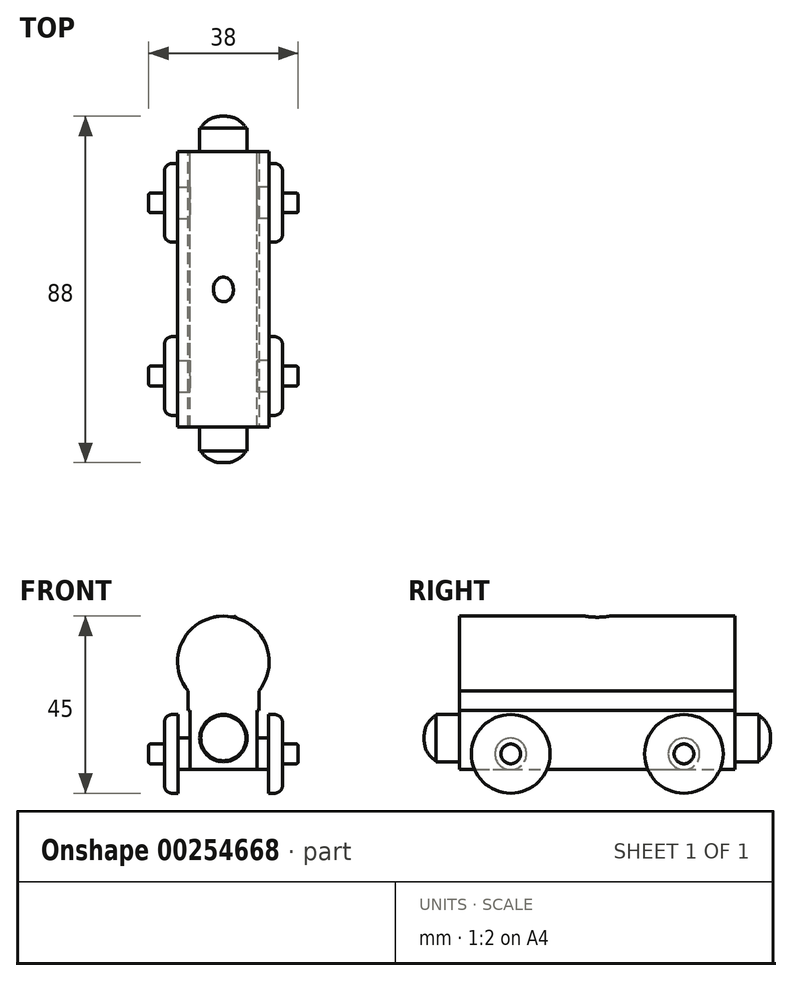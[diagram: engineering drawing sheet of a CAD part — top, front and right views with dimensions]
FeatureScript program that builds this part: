
annotation { "Feature Type Name" : "Feature", "Feature Type Description" : "" }
export const myFeature = defineFeature(function(context is Context, id is Id, definition is map)
    precondition{}
    {
        {
            var Q0;
            Q0=qCreatedBy(makeId("Front.planeOp"),FACE);
            var sketch = newSketch(context, id + "F0", { "sketchPlane" : qUnion([Q0])});
            skLineSegment(sketch, "E0", {"start": v(-9, -7.37) * mm, "end": v(9, -7.37) * mm});
            skArc(sketch, "E1", {"start": v(9, -7.37) * mm, "mid": v(0, 11.63) * mm, "end": v(-9, -7.37) * mm});
            skLineSegment(sketch, "E2", {"start": v(0, 19.14) * mm, "end": v(0, -28.25) * mm, "construction": true});
            skPoint(sketch, "E2.startSnap0", {"position": v(0, 11.63) * mm});
            skSolve(sketch);
        }
        {
            var Q0;
            Q0 = qSketchRegion(id + "F0", true);
            extrude(context, id + "F1", {"entities" : qUnion([Q0]), "endBound" : BoundingType.SYMMETRIC, "depth" : 70 * mm});
        }
        {
            var Q0;
            Q0=makeQuery(id+"F1.opExtrude","CAP_FACE",FACE,{"disambiguationData":[OSD([sQuery(id+"F0.wireOp",EDGE,"E0"),sQuery(id+"F0.wireOp",EDGE,"E1")])],"isStart":false});
            var sketch = newSketch(context, id + "F2", { "sketchPlane" : qUnion([Q0])});
            skLineSegment(sketch, "E3.bottom", {"start": v(-9, -7.37) * mm, "end": v(9, -7.37) * mm});
            skLineSegment(sketch, "E3.top", {"start": v(-9, -12.37) * mm, "end": v(9, -12.37) * mm});
            skLineSegment(sketch, "E3.left", {"start": v(-9, -7.37) * mm, "end": v(-9, -12.37) * mm});
            skLineSegment(sketch, "E3.right", {"start": v(9, -7.37) * mm, "end": v(9, -12.37) * mm});
            skSolve(sketch);
        }
        {
            var Q0;
            Q0 = qSketchRegion(id + "F2", true);
            extrude(context, id + "F3", {"entities" : qUnion([Q0]), "oppositeDirection" : true, "depth" : 70 * mm});
        }
        {
            var Q0;
            Q0=makeQuery(id+"F1.opExtrude","SWEPT_BODY",BODY,{"disambiguationData":[OSD([sQuery(id+"F0.wireOp",EDGE,"E0"),sQuery(id+"F0.wireOp",EDGE,"E1")])]});
            var Q1;
            Q1=makeQuery(id+"F3.opExtrude","SWEPT_BODY",BODY,{"disambiguationData":[OSD([sQuery(id+"F2.wireOp",EDGE,"E3.bottom"),sQuery(id+"F2.wireOp",EDGE,"E3.top"),sQuery(id+"F2.wireOp",EDGE,"E3.left"),sQuery(id+"F2.wireOp",EDGE,"E3.right")])]});
            booleanBodies(context, id + "F4", {"operationType" : BooleanOperationType.UNION, "tools" : qUnion([Q0, Q1])});
        }
        {
            var Q0;
            Q0=makeQuery(id+"F3.opExtrude","SWEPT_FACE",FACE,{"disambiguationData":[OSD([sQuery(id+"F2.wireOp",EDGE,"E3.top")])]});
            var sketch = newSketch(context, id + "F5", { "sketchPlane" : qUnion([Q0])});
            skLineSegment(sketch, "E4.bottom", {"start": v(-8.5, 35) * mm, "end": v(8.5, 35) * mm});
            skLineSegment(sketch, "E4.top", {"start": v(-8.5, -35) * mm, "end": v(8.5, -35) * mm});
            skLineSegment(sketch, "E4.left", {"start": v(-8.5, 35) * mm, "end": v(-8.5, -35) * mm});
            skLineSegment(sketch, "E4.right", {"start": v(8.5, 35) * mm, "end": v(8.5, -35) * mm});
            skSolve(sketch);
        }
        {
            var Q0;
            Q0 = qSketchRegion(id + "F5", true);
            extrude(context, id + "F6", {"entities" : qUnion([Q0]), "operationType" : NewBodyOperationType.ADD, "depth" : 15 * mm});
        }
        {
            var Q0;
            Q0=makeQuery(id+"F6.boolean.opBoolean","MERGE",FACE,{"derivedFrom":[makeQuery(id+"F4.opBoolean","MERGE",FACE,{"derivedFrom":[makeQuery(id+"F1.opExtrude","CAP_FACE",FACE,{"disambiguationData":[OSD([sQuery(id+"F0.wireOp",EDGE,"E0"),sQuery(id+"F0.wireOp",EDGE,"E1")])],"isStart":false}),makeQuery(id+"F3.opExtrude","CAP_FACE",FACE,{"disambiguationData":[OSD([sQuery(id+"F2.wireOp",EDGE,"E3.bottom"),sQuery(id+"F2.wireOp",EDGE,"E3.top"),sQuery(id+"F2.wireOp",EDGE,"E3.left"),sQuery(id+"F2.wireOp",EDGE,"E3.right")])],"isStart":true})]}),makeQuery(id+"F6.opExtrude","SWEPT_FACE",FACE,{"disambiguationData":[OSD([sQuery(id+"F5.wireOp",EDGE,"E4.bottom")])]})]});
            var sketch = newSketch(context, id + "F7", { "sketchPlane" : qUnion([Q0])});
            skCircle(sketch, "E5", {"center": v(0, -19.37) * mm, "radius": 6 * mm});
            skSolve(sketch);
        }
        {
            var Q0;
            Q0 = qSketchRegion(id + "F7", true);
            extrude(context, id + "F8", {"entities" : qUnion([Q0]), "operationType" : NewBodyOperationType.ADD, "depth" : 6 * mm});
        }
        {
            var Q0;
            Q0=makeQuery(id+"F6.boolean.opBoolean","MERGE",FACE,{"derivedFrom":[makeQuery(id+"F4.opBoolean","MERGE",FACE,{"derivedFrom":[makeQuery(id+"F1.opExtrude","CAP_FACE",FACE,{"disambiguationData":[OSD([sQuery(id+"F0.wireOp",EDGE,"E0"),sQuery(id+"F0.wireOp",EDGE,"E1")])],"isStart":true}),makeQuery(id+"F3.opExtrude","CAP_FACE",FACE,{"disambiguationData":[OSD([sQuery(id+"F2.wireOp",EDGE,"E3.bottom"),sQuery(id+"F2.wireOp",EDGE,"E3.top"),sQuery(id+"F2.wireOp",EDGE,"E3.left"),sQuery(id+"F2.wireOp",EDGE,"E3.right")])],"isStart":false})]}),makeQuery(id+"F6.opExtrude","SWEPT_FACE",FACE,{"disambiguationData":[OSD([sQuery(id+"F5.wireOp",EDGE,"E4.top")])]})]});
            var sketch = newSketch(context, id + "F9", { "sketchPlane" : qUnion([Q0])});
            skCircle(sketch, "E6", {"center": v(0, -19.37) * mm, "radius": 6 * mm});
            skSolve(sketch);
        }
        {
            var Q0;
            Q0 = qSketchRegion(id + "F9", true);
            extrude(context, id + "F10", {"entities" : qUnion([Q0]), "operationType" : NewBodyOperationType.ADD, "depth" : 6 * mm});
        }
        {
            var Q0;
            Q0=qCreatedBy(makeId("Front.planeOp"),FACE);
            var sketch = newSketch(context, id + "F11", { "sketchPlane" : qUnion([Q0])});
            skPoint(sketch, "E7.0", {"position": v(0, 11.63) * mm});
            skLineSegment(sketch, "E8", {"start": v(0, 11.63) * mm, "end": v(0, 16.63) * mm});
            skArc(sketch, "E9", {"start": v(0, 16.63) * mm, "mid": v(-4.5, 14.13) * mm, "end": v(0, 11.63) * mm});
            skSolve(sketch);
        }
        {
            var Q0;
            Q0 = qSketchRegion(id + "F11", true);
            var Q1;
            Q1=sQuery(id+"F0.wireOp",EDGE,"E2");
            revolve(context, id + "F12", {"operationType" : NewBodyOperationType.ADD, "entities" : qUnion([Q0]), "axis" : qUnion([Q1]), "revolveType" : RevolveType.FULL});
        }
        {
            var Q0;
            Q0=makeQuery(id+"F6.opExtrude","SWEPT_FACE",FACE,{"disambiguationData":[OSD([sQuery(id+"F5.wireOp",EDGE,"E4.right")])]});
            var sketch = newSketch(context, id + "F13", { "sketchPlane" : qUnion([Q0])});
            skCircle(sketch, "E10", {"center": v(-22, -23.37) * mm, "radius": 4 * mm});
            skSolve(sketch);
        }
        {
            var Q0;
            Q0 = qSketchRegion(id + "F13", true);
            extrude(context, id + "F14", {"entities" : qUnion([Q0]), "operationType" : NewBodyOperationType.ADD, "depth" : 3 * mm});
        }
        {
            var Q0;
            Q0=makeQuery(id+"F6.opExtrude","SWEPT_FACE",FACE,{"disambiguationData":[OSD([sQuery(id+"F5.wireOp",EDGE,"E4.right")])]});
            var sketch = newSketch(context, id + "F15", { "sketchPlane" : qUnion([Q0])});
            skCircle(sketch, "E11", {"center": v(22, -23.37) * mm, "radius": 4 * mm});
            skSolve(sketch);
        }
        {
            var Q0;
            Q0 = qSketchRegion(id + "F15", true);
            extrude(context, id + "F16", {"entities" : qUnion([Q0]), "operationType" : NewBodyOperationType.ADD, "depth" : 3 * mm});
        }
        {
            var Q0;
            Q0=makeQuery(id+"F6.opExtrude","SWEPT_FACE",FACE,{"disambiguationData":[OSD([sQuery(id+"F5.wireOp",EDGE,"E4.left")])]});
            var sketch = newSketch(context, id + "F17", { "sketchPlane" : qUnion([Q0])});
            skCircle(sketch, "E12", {"center": v(22, -23.37) * mm, "radius": 4 * mm});
            skSolve(sketch);
        }
        {
            var Q0;
            Q0 = qSketchRegion(id + "F17", true);
            extrude(context, id + "F18", {"entities" : qUnion([Q0]), "operationType" : NewBodyOperationType.ADD, "depth" : 3 * mm});
        }
        {
            var Q0;
            Q0=makeQuery(id+"F6.opExtrude","SWEPT_FACE",FACE,{"disambiguationData":[OSD([sQuery(id+"F5.wireOp",EDGE,"E4.left")])]});
            var sketch = newSketch(context, id + "F19", { "sketchPlane" : qUnion([Q0])});
            skCircle(sketch, "E13", {"center": v(-22, -23.37) * mm, "radius": 4 * mm});
            skSolve(sketch);
        }
        {
            var Q0;
            Q0 = qSketchRegion(id + "F19", true);
            extrude(context, id + "F20", {"entities" : qUnion([Q0]), "operationType" : NewBodyOperationType.ADD, "depth" : 3 * mm});
        }
        {
            var Q0;
            Q0=makeQuery(id+"F20.opExtrude","CAP_FACE",FACE,{"disambiguationData":[OSD([sQuery(id+"F19.wireOp",EDGE,"E13")])],"isStart":false});
            var sketch = newSketch(context, id + "F21", { "sketchPlane" : qUnion([Q0])});
            skCircle(sketch, "E14", {"center": v(-22, -23.37) * mm, "radius": 10 * mm});
            skSolve(sketch);
        }
        {
            var Q0;
            Q0 = qSketchRegion(id + "F21", true);
            extrude(context, id + "F22", {"entities" : qUnion([Q0]), "operationType" : NewBodyOperationType.ADD, "depth" : 3.5 * mm});
        }
        {
            var Q0;
            Q0=makeQuery(id+"F18.opExtrude","CAP_FACE",FACE,{"disambiguationData":[OSD([sQuery(id+"F17.wireOp",EDGE,"E12")])],"isStart":false});
            var sketch = newSketch(context, id + "F23", { "sketchPlane" : qUnion([Q0])});
            skCircle(sketch, "E15", {"center": v(22, -23.37) * mm, "radius": 10 * mm});
            skSolve(sketch);
        }
        {
            var Q0;
            Q0 = qSketchRegion(id + "F23", true);
            extrude(context, id + "F24", {"entities" : qUnion([Q0]), "operationType" : NewBodyOperationType.ADD, "depth" : 3.5 * mm});
        }
        {
            var Q0;
            Q0=makeQuery(id+"F14.opExtrude","CAP_FACE",FACE,{"disambiguationData":[OSD([sQuery(id+"F13.wireOp",EDGE,"E10")])],"isStart":false});
            var sketch = newSketch(context, id + "F25", { "sketchPlane" : qUnion([Q0])});
            skCircle(sketch, "E16", {"center": v(-22, -23.37) * mm, "radius": 10 * mm});
            skSolve(sketch);
        }
        {
            var Q0;
            Q0 = qSketchRegion(id + "F25", true);
            extrude(context, id + "F26", {"entities" : qUnion([Q0]), "operationType" : NewBodyOperationType.ADD, "depth" : 3.5 * mm});
        }
        {
            var Q0;
            Q0=makeQuery(id+"F16.opExtrude","CAP_FACE",FACE,{"disambiguationData":[OSD([sQuery(id+"F15.wireOp",EDGE,"E11")])],"isStart":false});
            var sketch = newSketch(context, id + "F27", { "sketchPlane" : qUnion([Q0])});
            skCircle(sketch, "E17", {"center": v(22, -23.37) * mm, "radius": 10 * mm});
            skSolve(sketch);
        }
        {
            var Q0;
            Q0 = qSketchRegion(id + "F27", true);
            extrude(context, id + "F28", {"entities" : qUnion([Q0]), "operationType" : NewBodyOperationType.ADD, "depth" : 3.5 * mm});
        }
        {
            var Q0;
            Q0=makeQuery(id+"F26.opExtrude","CAP_FACE",FACE,{"disambiguationData":[OSD([sQuery(id+"F25.wireOp",EDGE,"E16")])],"isStart":false});
            var sketch = newSketch(context, id + "F29", { "sketchPlane" : qUnion([Q0])});
            skCircle(sketch, "E18", {"center": v(-22, -23.37) * mm, "radius": 2.5 * mm});
            skSolve(sketch);
        }
        {
            var Q0;
            Q0 = qSketchRegion(id + "F29", true);
            extrude(context, id + "F30", {"entities" : qUnion([Q0]), "operationType" : NewBodyOperationType.ADD, "depth" : 4 * mm});
        }
        {
            var Q0;
            Q0=makeQuery(id+"F28.opExtrude","CAP_FACE",FACE,{"disambiguationData":[OSD([sQuery(id+"F27.wireOp",EDGE,"E17")])],"isStart":false});
            var sketch = newSketch(context, id + "F31", { "sketchPlane" : qUnion([Q0])});
            skCircle(sketch, "E19", {"center": v(22, -23.37) * mm, "radius": 2.5 * mm});
            skSolve(sketch);
        }
        {
            var Q0;
            Q0 = qSketchRegion(id + "F31", true);
            extrude(context, id + "F32", {"entities" : qUnion([Q0]), "operationType" : NewBodyOperationType.ADD, "depth" : 4 * mm});
        }
        {
            var Q0;
            Q0=makeQuery(id+"F22.opExtrude","CAP_FACE",FACE,{"disambiguationData":[OSD([sQuery(id+"F21.wireOp",EDGE,"E14")])],"isStart":false});
            var sketch = newSketch(context, id + "F33", { "sketchPlane" : qUnion([Q0])});
            skCircle(sketch, "E20", {"center": v(-22, -23.37) * mm, "radius": 2.5 * mm});
            skSolve(sketch);
        }
        {
            var Q0;
            Q0 = qSketchRegion(id + "F33", true);
            extrude(context, id + "F34", {"entities" : qUnion([Q0]), "operationType" : NewBodyOperationType.ADD, "depth" : 4 * mm});
        }
        {
            var Q0;
            Q0=makeQuery(id+"F24.opExtrude","CAP_FACE",FACE,{"disambiguationData":[OSD([sQuery(id+"F23.wireOp",EDGE,"E15")])],"isStart":false});
            var sketch = newSketch(context, id + "F35", { "sketchPlane" : qUnion([Q0])});
            skCircle(sketch, "E21", {"center": v(22, -23.37) * mm, "radius": 2.5 * mm});
            skSolve(sketch);
        }
        {
            var Q0;
            Q0 = qSketchRegion(id + "F35", true);
            extrude(context, id + "F36", {"entities" : qUnion([Q0]), "operationType" : NewBodyOperationType.ADD, "depth" : 4 * mm});
        }
        {
            var Q0;
            Q0=makeQuery(id+"F22.opExtrude","CAP_EDGE",EDGE,{"disambiguationData":[OSD([sQuery(id+"F21.wireOp",EDGE,"E14")])],"isStart":false});
            fillet(context, id + "F37", {"entities" : qUnion([Q0]), "radius" : 2 * mm, "tangentPropagation" : true, "allowEdgeOverflow" : false});
        }
        {
            var Q0;
            Q0=makeQuery(id+"F24.opExtrude","CAP_EDGE",EDGE,{"disambiguationData":[OSD([sQuery(id+"F23.wireOp",EDGE,"E15")])],"isStart":false});
            fillet(context, id + "F38", {"entities" : qUnion([Q0]), "radius" : 2 * mm, "tangentPropagation" : true, "allowEdgeOverflow" : false});
        }
        {
            var Q0;
            Q0=makeQuery(id+"F26.opExtrude","CAP_EDGE",EDGE,{"disambiguationData":[OSD([sQuery(id+"F25.wireOp",EDGE,"E16")])],"isStart":false});
            fillet(context, id + "F39", {"entities" : qUnion([Q0]), "radius" : 2 * mm, "tangentPropagation" : true, "allowEdgeOverflow" : false});
        }
        {
            var Q0;
            Q0=makeQuery(id+"F28.opExtrude","CAP_EDGE",EDGE,{"disambiguationData":[OSD([sQuery(id+"F27.wireOp",EDGE,"E17")])],"isStart":false});
            fillet(context, id + "F40", {"entities" : qUnion([Q0]), "radius" : 2 * mm, "tangentPropagation" : true, "allowEdgeOverflow" : false});
        }
        {
            var Q0;
            Q0=makeQuery(id+"F10.opExtrude","CAP_FACE",FACE,{"disambiguationData":[OSD([sQuery(id+"F9.wireOp",EDGE,"E6")])],"isStart":false});
            var sketch = newSketch(context, id + "F41", { "sketchPlane" : qUnion([Q0])});
            skCircle(sketch, "E22", {"center": v(0, -19.37) * mm, "radius": 5.75 * mm});
            skSolve(sketch);
        }
        {
            var Q0;
            Q0 = qSketchRegion(id + "F41", true);
            extrude(context, id + "F42", {"entities" : qUnion([Q0]), "operationType" : NewBodyOperationType.ADD, "depth" : 3 * mm});
        }
        {
            var Q0;
            Q0=makeQuery(id+"F42.opExtrude","CAP_EDGE",EDGE,{"disambiguationData":[OSD([sQuery(id+"F41.wireOp",EDGE,"E22")])],"isStart":false});
            fillet(context, id + "F43", {"entities" : qUnion([Q0]), "radius" : 6 * mm, "tangentPropagation" : true, "allowEdgeOverflow" : false});
        }
        {
            var Q0;
            Q0=makeQuery(id+"F8.opExtrude","CAP_FACE",FACE,{"disambiguationData":[OSD([sQuery(id+"F7.wireOp",EDGE,"E5")])],"isStart":false});
            var sketch = newSketch(context, id + "F44", { "sketchPlane" : qUnion([Q0])});
            skCircle(sketch, "E23", {"center": v(0, -19.37) * mm, "radius": 5.75 * mm});
            skSolve(sketch);
        }
        {
            var Q0;
            Q0 = qSketchRegion(id + "F44", true);
            extrude(context, id + "F45", {"entities" : qUnion([Q0]), "operationType" : NewBodyOperationType.ADD, "depth" : 3 * mm});
        }
        {
            var Q0;
            Q0=makeQuery(id+"F45.opExtrude","CAP_EDGE",EDGE,{"disambiguationData":[OSD([sQuery(id+"F44.wireOp",EDGE,"E23")])],"isStart":false});
            fillet(context, id + "F46", {"entities" : qUnion([Q0]), "radius" : 6 * mm, "tangentPropagation" : true, "allowEdgeOverflow" : false});
        }
        {
            var Q0;
            Q0=makeQuery(id+"F36.opExtrude","CAP_EDGE",EDGE,{"disambiguationData":[OSD([sQuery(id+"F35.wireOp",EDGE,"E21")])],"isStart":false});
            fillet(context, id + "F47", {"entities" : qUnion([Q0]), "radius" : 0.5 * mm, "tangentPropagation" : true, "allowEdgeOverflow" : false});
        }
        {
            var Q0;
            Q0=makeQuery(id+"F34.opExtrude","CAP_EDGE",EDGE,{"disambiguationData":[OSD([sQuery(id+"F33.wireOp",EDGE,"E20")])],"isStart":false});
            fillet(context, id + "F48", {"entities" : qUnion([Q0]), "radius" : 0.5 * mm, "tangentPropagation" : true, "allowEdgeOverflow" : false});
        }
        {
            var Q0;
            Q0=makeQuery(id+"F30.opExtrude","CAP_EDGE",EDGE,{"disambiguationData":[OSD([sQuery(id+"F29.wireOp",EDGE,"E18")])],"isStart":false});
            fillet(context, id + "F49", {"entities" : qUnion([Q0]), "radius" : 0.5 * mm, "tangentPropagation" : true, "allowEdgeOverflow" : false});
        }
        {
            var Q0;
            Q0=makeQuery(id+"F32.opExtrude","CAP_EDGE",EDGE,{"disambiguationData":[OSD([sQuery(id+"F31.wireOp",EDGE,"E19")])],"isStart":false});
            fillet(context, id + "F50", {"entities" : qUnion([Q0]), "radius" : 0.5 * mm, "tangentPropagation" : true, "allowEdgeOverflow" : false});
        }
    });
